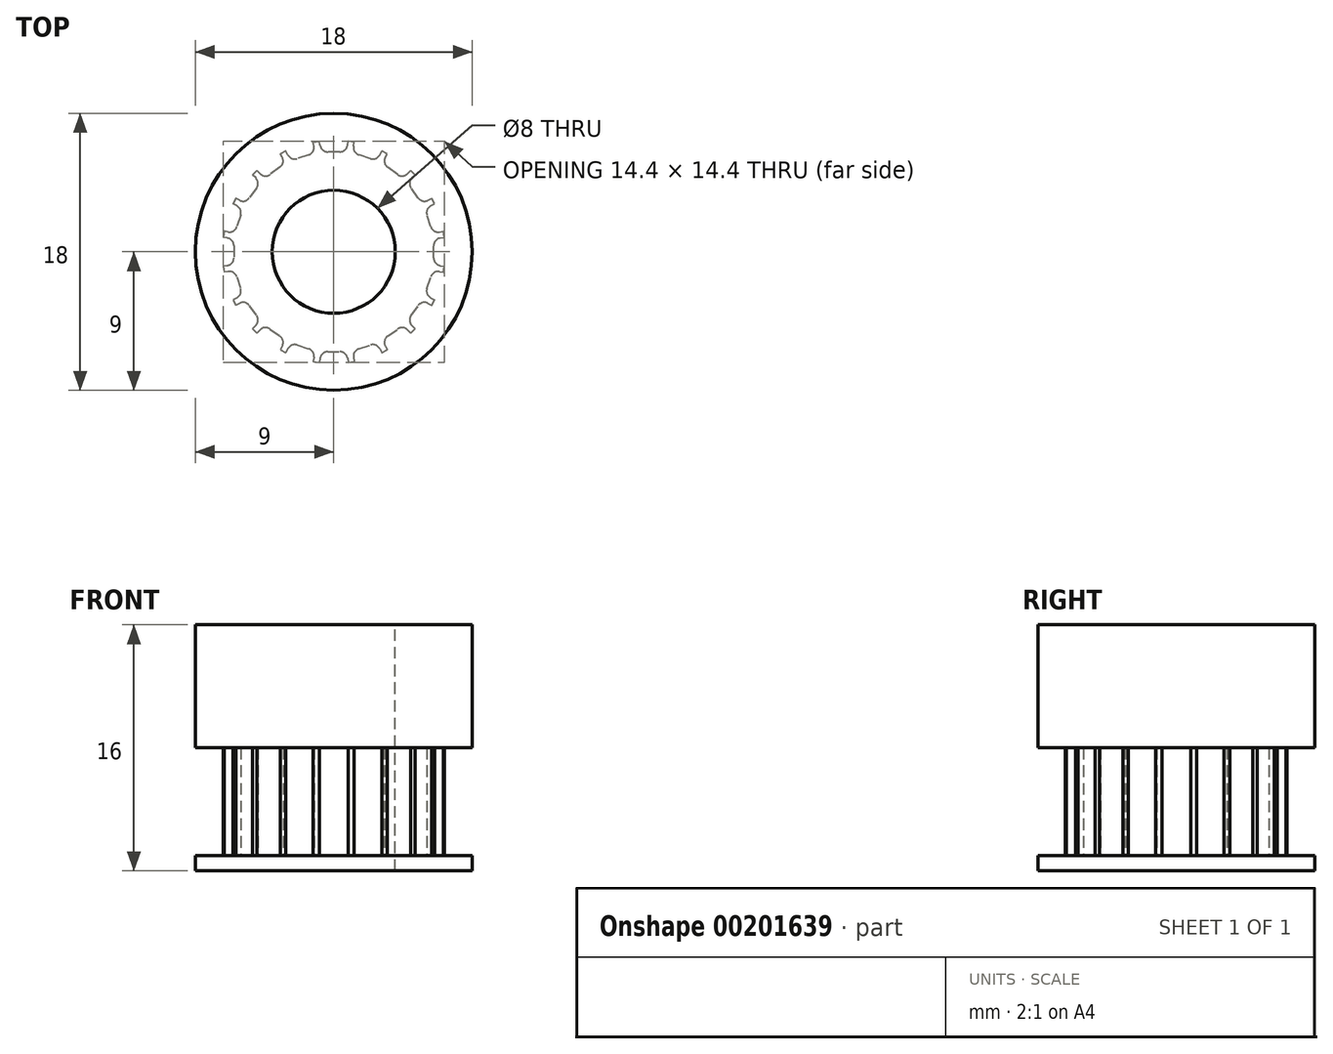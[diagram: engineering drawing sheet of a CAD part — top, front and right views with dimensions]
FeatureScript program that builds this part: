
annotation { "Feature Type Name" : "Feature", "Feature Type Description" : "" }
export const myFeature = defineFeature(function(context is Context, id is Id, definition is map)
    precondition{}
    {
        {
            var Q0;
            Q0=qCreatedBy(makeId("Top.planeOp"),FACE);
            var sketch = newSketch(context, id + "F0", { "sketchPlane" : qUnion([Q0])});
            skCircle(sketch, "E0", {"center": v(0, 0) * mm, "radius": 6.5 * mm, "construction": true});
            skLineSegment(sketch, "E1", {"start": v(0, 0) * mm, "end": v(0, 6.5) * mm, "construction": true});
            skLineSegment(sketch, "E2", {"start": v(0, 0) * mm, "end": v(-1.14, 7.17) * mm});
            skCircle(sketch, "E3", {"center": v(0, 0) * mm, "radius": 7.26 * mm, "construction": true});
            skLineSegment(sketch, "E4", {"start": v(-0.4, 6.5) * mm, "end": v(0, 6.5) * mm});
            skLineSegment(sketch, "E5.0", {"start": v(-0.9, 6.92) * mm, "end": v(-0.94, 7.2) * mm});
            skLineSegment(sketch, "E6.MirrorCS", {"start": v(0.82, 6.45) * mm, "end": v(0.83, 6.5) * mm});
            skPoint(sketch, "E7.newPointB", {"position": v(-0.82, 6.45) * mm});
            skArc(sketch, "E7.filletArc", {"start": v(-0.9, 6.92) * mm, "mid": v(-0.72, 6.62) * mm, "end": v(-0.4, 6.5) * mm});
            skLineSegment(sketch, "E8", {"start": v(-1.14, 7.17) * mm, "end": v(-0.94, 7.2) * mm});
            skPoint(sketch, "E9.MirrorCS.end.orphan", {"position": v(1.14, 7.17) * mm});
            skLineSegment(sketch, "E10.trimOffspring", {"start": v(0.94, 7.2) * mm, "end": v(0.94, 7.2) * mm});
            skLineSegment(sketch, "E11.MirrorCS", {"start": v(0, 0) * mm, "end": v(1.14, 7.17) * mm});
            skLineSegment(sketch, "E12.MirrorCS", {"start": v(0.9, 6.92) * mm, "end": v(0.94, 7.2) * mm});
            skArc(sketch, "E13.MirrorCS", {"start": v(0.9, 6.92) * mm, "mid": v(0.72, 6.62) * mm, "end": v(0.4, 6.5) * mm});
            skLineSegment(sketch, "E14.MirrorCS", {"start": v(0.4, 6.5) * mm, "end": v(0, 6.5) * mm});
            skLineSegment(sketch, "E15.MirrorCS", {"start": v(1.14, 7.17) * mm, "end": v(0.94, 7.2) * mm});
            skSolve(sketch);
        }
        {
            var Q0;
            Q0=makeQuery(id+"F0.imprint","IMPRINT",FACE,{"disambiguationData":[TD([[makeQuery(id+"F0.imprint","IMPRINT",EDGE,{"derivedFrom":sQuery(id+"F0.wireOp",EDGE,"E2")}),-1.0]])]});
            extrude(context, id + "F1", {"entities" : qUnion([Q0]), "endBound" : BoundingType.SYMMETRIC, "depth" : 7 * mm});
        }
        {
            var Q0;
            Q0=makeQuery(id+"F1.opExtrude","SWEPT_BODY",BODY,{"disambiguationData":[OSD([sQuery(id+"F0.wireOp",EDGE,"E2"),sQuery(id+"F0.wireOp",EDGE,"E4"),sQuery(id+"F0.wireOp",EDGE,"E5.0"),sQuery(id+"F0.wireOp",EDGE,"E7.filletArc"),sQuery(id+"F0.wireOp",EDGE,"E8"),sQuery(id+"F0.wireOp",EDGE,"E11.MirrorCS"),sQuery(id+"F0.wireOp",EDGE,"E12.MirrorCS"),sQuery(id+"F0.wireOp",EDGE,"E13.MirrorCS"),sQuery(id+"F0.wireOp",EDGE,"E14.MirrorCS"),sQuery(id+"F0.wireOp",EDGE,"E15.MirrorCS")])]});
            var Q1;
            Q1=makeQuery(id+"F1.opExtrude","SWEPT_EDGE",EDGE,{"disambiguationData":[OSD([sQuery(id+"F0.wireOp",EDGE,"E2"),sQuery(id+"F0.wireOp",EDGE,"E11.MirrorCS")])]});
            circularPattern(context, id + "F2", {"operationType" : NewBodyOperationType.ADD, "entities" : qUnion([Q0]), "axis" : qUnion([Q1]), "angle" : 360 * degree, "instanceCount" : 20, "equalSpace" : true});
        }
        {
            var Q0;
            {var subQ0=makeQuery(id+"F1.opExtrude","CAP_FACE",FACE,{"disambiguationData":[OSD([sQuery(id+"F0.wireOp",EDGE,"E2"),sQuery(id+"F0.wireOp",EDGE,"E4"),sQuery(id+"F0.wireOp",EDGE,"E5.0"),sQuery(id+"F0.wireOp",EDGE,"E7.filletArc"),sQuery(id+"F0.wireOp",EDGE,"E8"),sQuery(id+"F0.wireOp",EDGE,"E11.MirrorCS"),sQuery(id+"F0.wireOp",EDGE,"E12.MirrorCS"),sQuery(id+"F0.wireOp",EDGE,"E13.MirrorCS"),sQuery(id+"F0.wireOp",EDGE,"E14.MirrorCS"),sQuery(id+"F0.wireOp",EDGE,"E15.MirrorCS")])],"isStart":true});Q0=makeQuery(id+"F2.boolean.opBoolean","MERGE",FACE,{"derivedFrom":[subQ0,makeQuery(id+"F2.opPattern","COPY",FACE,{"derivedFrom":subQ0,"instanceName":"1"}),makeQuery(id+"F2.opPattern","COPY",FACE,{"derivedFrom":subQ0,"instanceName":"2"}),makeQuery(id+"F2.opPattern","COPY",FACE,{"derivedFrom":subQ0,"instanceName":"3"}),makeQuery(id+"F2.opPattern","COPY",FACE,{"derivedFrom":subQ0,"instanceName":"4"}),makeQuery(id+"F2.opPattern","COPY",FACE,{"derivedFrom":subQ0,"instanceName":"5"}),makeQuery(id+"F2.opPattern","COPY",FACE,{"derivedFrom":subQ0,"instanceName":"6"}),makeQuery(id+"F2.opPattern","COPY",FACE,{"derivedFrom":subQ0,"instanceName":"7"}),makeQuery(id+"F2.opPattern","COPY",FACE,{"derivedFrom":subQ0,"instanceName":"8"}),makeQuery(id+"F2.opPattern","COPY",FACE,{"derivedFrom":subQ0,"instanceName":"9"}),makeQuery(id+"F2.opPattern","COPY",FACE,{"derivedFrom":subQ0,"instanceName":"10"}),makeQuery(id+"F2.opPattern","COPY",FACE,{"derivedFrom":subQ0,"instanceName":"11"}),makeQuery(id+"F2.opPattern","COPY",FACE,{"derivedFrom":subQ0,"instanceName":"12"}),makeQuery(id+"F2.opPattern","COPY",FACE,{"derivedFrom":subQ0,"instanceName":"13"}),makeQuery(id+"F2.opPattern","COPY",FACE,{"derivedFrom":subQ0,"instanceName":"14"}),makeQuery(id+"F2.opPattern","COPY",FACE,{"derivedFrom":subQ0,"instanceName":"15"}),makeQuery(id+"F2.opPattern","COPY",FACE,{"derivedFrom":subQ0,"instanceName":"16"}),makeQuery(id+"F2.opPattern","COPY",FACE,{"derivedFrom":subQ0,"instanceName":"17"}),makeQuery(id+"F2.opPattern","COPY",FACE,{"derivedFrom":subQ0,"instanceName":"18"}),makeQuery(id+"F2.opPattern","COPY",FACE,{"derivedFrom":subQ0,"instanceName":"19"})]});}
            var sketch = newSketch(context, id + "F3", { "sketchPlane" : qUnion([Q0])});
            skCircle(sketch, "E16", {"center": v(0, 0) * mm, "radius": 9 * mm});
            skSolve(sketch);
        }
        {
            var Q0;
            Q0=makeQuery(id+"F3.imprint","IMPRINT",FACE,{"disambiguationData":[TD([[makeQuery(id+"F3.imprint","IMPRINT",EDGE,{"derivedFrom":sQuery(id+"F3.wireOp",EDGE,"E16")}),1.0]])]});
            var Q1;
            {var subQ2=makeQuery(id+"F1.opExtrude","CAP_EDGE",EDGE,{"disambiguationData":[OSD([sQuery(id+"F0.wireOp",EDGE,"E5.0")])],"isStart":true});Q1=makeQuery(id+"F3.imprint","IMPRINT",FACE,{"disambiguationData":[TD([[makeQuery(id+"F3.imprint","IMPRINT",EDGE,{"derivedFrom":subQ2}),-1.0]])]});}
            extrude(context, id + "F4", {"entities" : qUnion([Q0, Q1]), "operationType" : NewBodyOperationType.ADD, "depth" : 1 * mm});
        }
        {
            var Q0;
            {var subQ0=makeQuery(id+"F1.opExtrude","CAP_FACE",FACE,{"disambiguationData":[OSD([sQuery(id+"F0.wireOp",EDGE,"E2"),sQuery(id+"F0.wireOp",EDGE,"E4"),sQuery(id+"F0.wireOp",EDGE,"E5.0"),sQuery(id+"F0.wireOp",EDGE,"E7.filletArc"),sQuery(id+"F0.wireOp",EDGE,"E8"),sQuery(id+"F0.wireOp",EDGE,"E11.MirrorCS"),sQuery(id+"F0.wireOp",EDGE,"E12.MirrorCS"),sQuery(id+"F0.wireOp",EDGE,"E13.MirrorCS"),sQuery(id+"F0.wireOp",EDGE,"E14.MirrorCS"),sQuery(id+"F0.wireOp",EDGE,"E15.MirrorCS")])],"isStart":false});Q0=makeQuery(id+"F2.boolean.opBoolean","MERGE",FACE,{"derivedFrom":[subQ0,makeQuery(id+"F2.opPattern","COPY",FACE,{"derivedFrom":subQ0,"instanceName":"1"}),makeQuery(id+"F2.opPattern","COPY",FACE,{"derivedFrom":subQ0,"instanceName":"2"}),makeQuery(id+"F2.opPattern","COPY",FACE,{"derivedFrom":subQ0,"instanceName":"3"}),makeQuery(id+"F2.opPattern","COPY",FACE,{"derivedFrom":subQ0,"instanceName":"4"}),makeQuery(id+"F2.opPattern","COPY",FACE,{"derivedFrom":subQ0,"instanceName":"5"}),makeQuery(id+"F2.opPattern","COPY",FACE,{"derivedFrom":subQ0,"instanceName":"6"}),makeQuery(id+"F2.opPattern","COPY",FACE,{"derivedFrom":subQ0,"instanceName":"7"}),makeQuery(id+"F2.opPattern","COPY",FACE,{"derivedFrom":subQ0,"instanceName":"8"}),makeQuery(id+"F2.opPattern","COPY",FACE,{"derivedFrom":subQ0,"instanceName":"9"}),makeQuery(id+"F2.opPattern","COPY",FACE,{"derivedFrom":subQ0,"instanceName":"10"}),makeQuery(id+"F2.opPattern","COPY",FACE,{"derivedFrom":subQ0,"instanceName":"11"}),makeQuery(id+"F2.opPattern","COPY",FACE,{"derivedFrom":subQ0,"instanceName":"12"}),makeQuery(id+"F2.opPattern","COPY",FACE,{"derivedFrom":subQ0,"instanceName":"13"}),makeQuery(id+"F2.opPattern","COPY",FACE,{"derivedFrom":subQ0,"instanceName":"14"}),makeQuery(id+"F2.opPattern","COPY",FACE,{"derivedFrom":subQ0,"instanceName":"15"}),makeQuery(id+"F2.opPattern","COPY",FACE,{"derivedFrom":subQ0,"instanceName":"16"}),makeQuery(id+"F2.opPattern","COPY",FACE,{"derivedFrom":subQ0,"instanceName":"17"}),makeQuery(id+"F2.opPattern","COPY",FACE,{"derivedFrom":subQ0,"instanceName":"18"}),makeQuery(id+"F2.opPattern","COPY",FACE,{"derivedFrom":subQ0,"instanceName":"19"})]});}
            var sketch = newSketch(context, id + "F5", { "sketchPlane" : qUnion([Q0])});
            skCircle(sketch, "E17.0", {"center": v(0, 0) * mm, "radius": 9 * mm});
            skSolve(sketch);
        }
        {
            var Q0;
            Q0=makeQuery(id+"F5.imprint","IMPRINT",FACE,{"disambiguationData":[TD([[makeQuery(id+"F5.imprint","IMPRINT",EDGE,{"derivedFrom":sQuery(id+"F5.wireOp",EDGE,"E17.0")}),1.0]])]});
            var Q1;
            {var subQ3=makeQuery(id+"F1.opExtrude","CAP_EDGE",EDGE,{"disambiguationData":[OSD([sQuery(id+"F0.wireOp",EDGE,"E5.0")])],"isStart":false});Q1=makeQuery(id+"F5.imprint","IMPRINT",FACE,{"disambiguationData":[TD([[makeQuery(id+"F5.imprint","IMPRINT",EDGE,{"derivedFrom":subQ3}),1.0]])]});}
            extrude(context, id + "F6", {"entities" : qUnion([Q0, Q1]), "operationType" : NewBodyOperationType.ADD, "depth" : 8 * mm});
        }
        {
            var Q0;
            Q0=makeQuery(id+"F6.opExtrude","CAP_FACE",FACE,{"disambiguationData":[OSD([sQuery(id+"F5.wireOp",EDGE,"E17.0")])],"isStart":false});
            var sketch = newSketch(context, id + "F7", { "sketchPlane" : qUnion([Q0])});
            skPoint(sketch, "E18", {"position": v(0, 0) * mm});
            skSolve(sketch);
        }
        {
            var Q0;
            Q0=sQuery(id+"F7.wireOp",VERTEX,"E18");
            var Q1;
            Q1=makeQuery(id+"F1.opExtrude","SWEPT_BODY",BODY,{"disambiguationData":[OSD([sQuery(id+"F0.wireOp",EDGE,"E2"),sQuery(id+"F0.wireOp",EDGE,"E4"),sQuery(id+"F0.wireOp",EDGE,"E5.0"),sQuery(id+"F0.wireOp",EDGE,"E7.filletArc"),sQuery(id+"F0.wireOp",EDGE,"E8"),sQuery(id+"F0.wireOp",EDGE,"E11.MirrorCS"),sQuery(id+"F0.wireOp",EDGE,"E12.MirrorCS"),sQuery(id+"F0.wireOp",EDGE,"E13.MirrorCS"),sQuery(id+"F0.wireOp",EDGE,"E14.MirrorCS"),sQuery(id+"F0.wireOp",EDGE,"E15.MirrorCS")])]});
            hole(context, id + "F8", {"style" : HoleStyle.SIMPLE, "holeDiameter" : 8 * mm, "endStyle" : HoleEndStyle.THROUGH, "locations" : qUnion([Q0]), "scope" : qUnion([Q1]), "isTappedThrough" : true});
        }
    });
